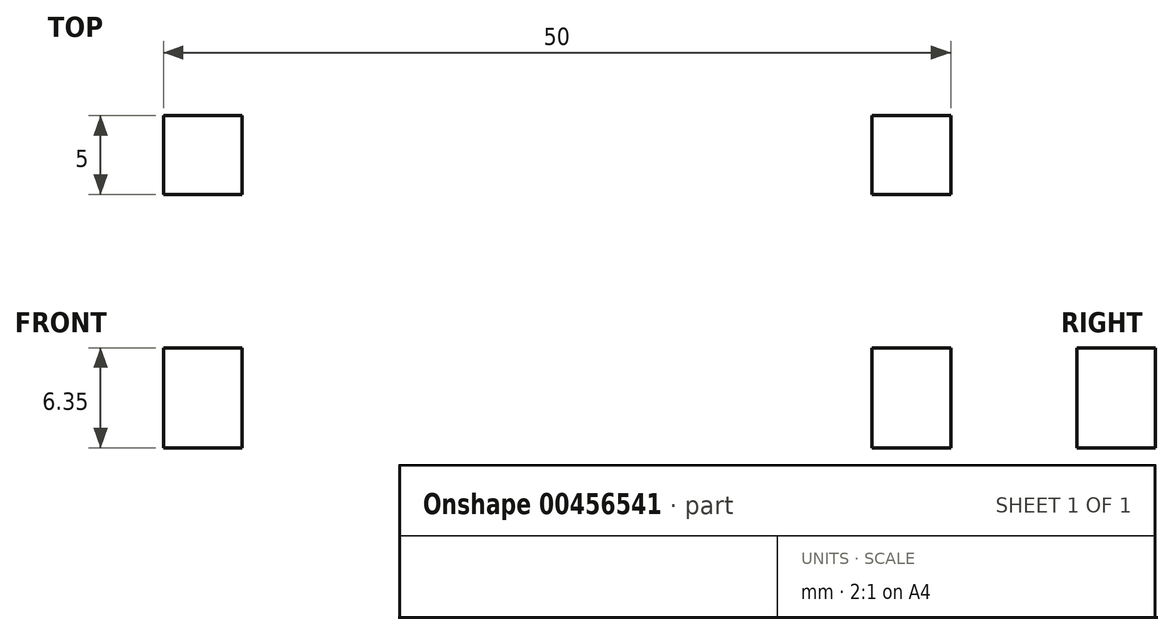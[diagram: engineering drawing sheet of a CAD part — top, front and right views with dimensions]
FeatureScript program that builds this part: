
annotation { "Feature Type Name" : "Feature", "Feature Type Description" : "" }
export const myFeature = defineFeature(function(context is Context, id is Id, definition is map)
    precondition{}
    {
        {
            var Q0;
            Q0=qCreatedBy(makeId("Top.planeOp"),FACE);
            var sketch = newSketch(context, id + "F0", { "sketchPlane" : qUnion([Q0])});
            skLineSegment(sketch, "E0.bottom", {"start": v(25, 50) * mm, "end": v(-25, 50) * mm});
            skLineSegment(sketch, "E0.top", {"start": v(25, -50) * mm, "end": v(-25, -50) * mm});
            skLineSegment(sketch, "E0.left", {"start": v(25, 50) * mm, "end": v(25, -50) * mm});
            skLineSegment(sketch, "E0.right", {"start": v(-25, 50) * mm, "end": v(-25, -50) * mm});
            skPoint(sketch, "E0.middle", {"position": v(0, 0) * mm});
            skCircle(sketch, "E1", {"center": v(0, 0) * mm, "radius": 3.12 * mm});
            skLineSegment(sketch, "E2.bottom", {"start": v(-25, 50) * mm, "end": v(-20, 50) * mm});
            skLineSegment(sketch, "E2.top", {"start": v(-25, 45) * mm, "end": v(-20, 45) * mm});
            skLineSegment(sketch, "E2.left", {"start": v(-25, 50) * mm, "end": v(-25, 45) * mm});
            skLineSegment(sketch, "E2.right", {"start": v(-20, 50) * mm, "end": v(-20, 45) * mm});
            skLineSegment(sketch, "E3.bottom", {"start": v(25, 50) * mm, "end": v(20, 50) * mm});
            skLineSegment(sketch, "E3.top", {"start": v(25, 45) * mm, "end": v(20, 45) * mm});
            skLineSegment(sketch, "E3.left", {"start": v(25, 50) * mm, "end": v(25, 45) * mm});
            skLineSegment(sketch, "E3.right", {"start": v(20, 50) * mm, "end": v(20, 45) * mm});
            skLineSegment(sketch, "E4.bottom", {"start": v(-25, -50) * mm, "end": v(-20, -50) * mm});
            skLineSegment(sketch, "E4.top", {"start": v(-25, -45) * mm, "end": v(-20, -45) * mm});
            skLineSegment(sketch, "E4.left", {"start": v(-25, -50) * mm, "end": v(-25, -45) * mm});
            skLineSegment(sketch, "E4.right", {"start": v(-20, -50) * mm, "end": v(-20, -45) * mm});
            skLineSegment(sketch, "E5.bottom", {"start": v(25, -50) * mm, "end": v(20, -50) * mm});
            skLineSegment(sketch, "E5.top", {"start": v(25, -45) * mm, "end": v(20, -45) * mm});
            skLineSegment(sketch, "E5.left", {"start": v(25, -50) * mm, "end": v(25, -45) * mm});
            skLineSegment(sketch, "E5.right", {"start": v(20, -50) * mm, "end": v(20, -45) * mm});
            skSolve(sketch);
        }
        {
            var Q0;
            Q0=makeQuery(id+"F0.imprint","IMPRINT",FACE,{"disambiguationData":[TD([[makeQuery(id+"F0.imprint","IMPRINT",EDGE,{"derivedFrom":sQuery(id+"F0.wireOp",EDGE,"E0.bottom")}),1.0]])]});
            extrude(context, id + "F1", {"entities" : qUnion([Q0]), "depth" : 6.35 * mm});
        }
    });
